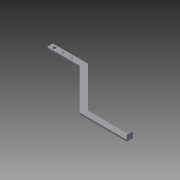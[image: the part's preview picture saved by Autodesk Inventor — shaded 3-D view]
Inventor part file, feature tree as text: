
AUTODESK INVENTOR PART (.ipt)
format: ipt  version: 2013 (Build 170138000, 138)  size: 166,912 bytes
history: native  units: in
note: dims shown in document units (in); Inventor stores cm internally (conversion verified against a paired STEP export)
features: extrude x8, sketch x7
ambient origin geometry x8: Origin, YZ Plane, XZ Plane, XY Plane, X Axis, Y Axis, Z Axis, Center Point
bodies: Solid1 (feature_tree)
feature tree (15):
  extrude  "Extrusion1"  Depth=1.0in
  extrude  "Extrusion2"  Depth=1.0in
  extrude  "Extrusion3"  Depth=9.336in
  extrude  "Extrusion5"  Depth=7.586in
  extrude  "Extrusion7"  Depth=0.25in TaperAngle=0.0deg
  extrude  "Extrusion8"  Depth=1.0in
  extrude  "Extrusion9"  Depth=1.75in TaperAngle=0.0deg
  extrude  "Extrusion10"  Depth=0.25in TaperAngle=0.0deg
  sketch  "Sketch1"  dims[d0=5.25in d1=1.0in]
  sketch  "Sketch3"  dims[d2=112.5deg d3=1.0in]
  sketch  "Sketch5"  dims[d4=135.0deg d5=9.336in]
  sketch  "Sketch7"  dims[d6=0.5in d7=7.586in]
  sketch  "Sketch8"  dims[d8=1.0in d9=0.25in d10=0.0in]
  sketch  "Sketch9"  dims[d13=0.0625in d14=0.0in d15=1.0in]
  sketch  "Sketch10"  dims[d16=1.0in d17=1.75in d18=0.0in d23=0.25in d24=0.0in d31=1.5in d32=180.0deg d33=3.0in d34=0.0in d35=0.25in d36=0.25in d37=1.0in d38=0.0in d39=1.75in d40=1.0in d41=1.5in d42=180.0deg d43=0.25in d44=1.0in d45=0.0in d46=0.25in d47=0.0in d48=0.25in d49=180.0deg d50=0.25in d51=0.0in]
